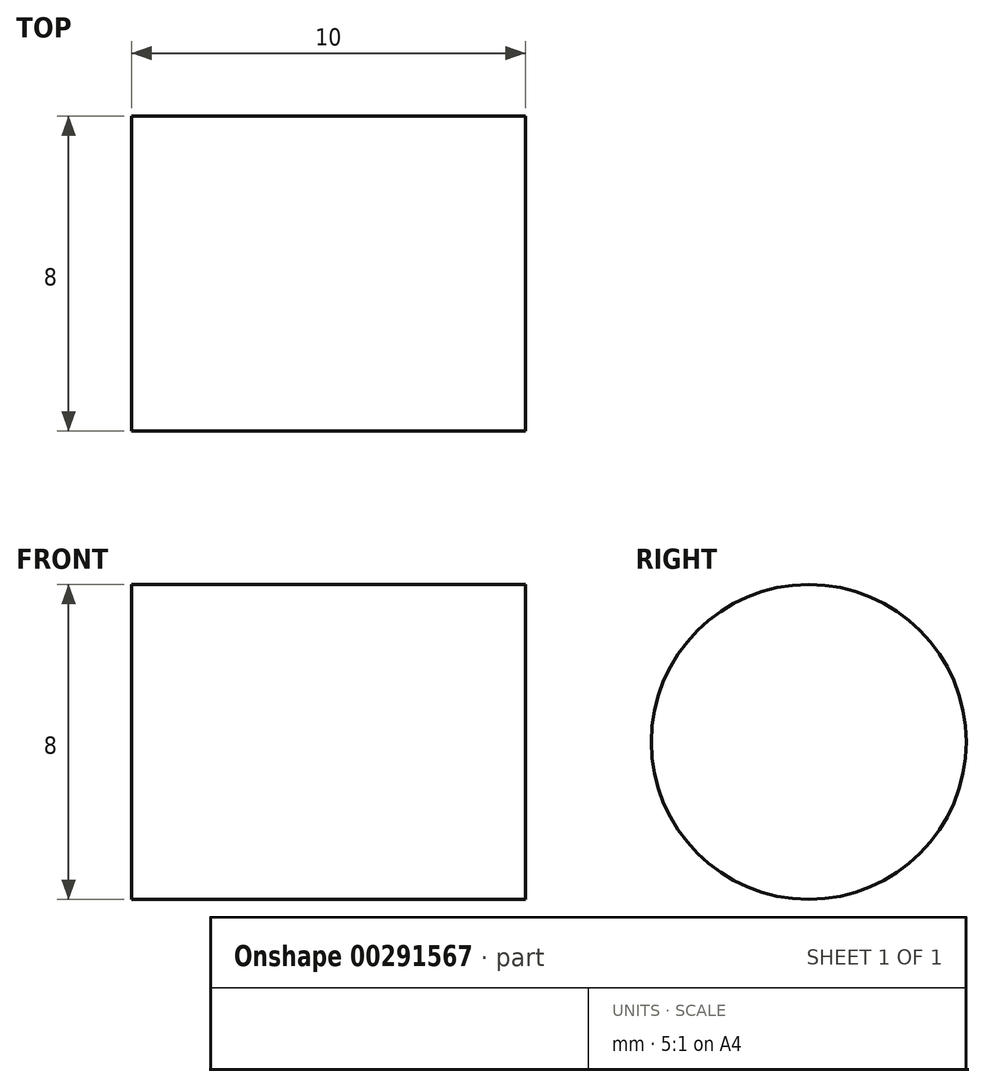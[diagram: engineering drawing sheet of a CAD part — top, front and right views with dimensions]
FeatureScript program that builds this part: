
annotation { "Feature Type Name" : "Feature", "Feature Type Description" : "" }
export const myFeature = defineFeature(function(context is Context, id is Id, definition is map)
    precondition{}
    {
        {
            var Q0;
            Q0=qCreatedBy(makeId("Right.planeOp"),FACE);
            var sketch = newSketch(context, id + "F0", { "sketchPlane" : qUnion([Q0])});
            skCircle(sketch, "E0", {"center": v(0, 0) * mm, "radius": 4 * mm});
            skSolve(sketch);
        }
        {
            var Q0;
            Q0 = qSketchRegion(id + "F0", true);
            extrude(context, id + "F1", {"entities" : qUnion([Q0]), "depth" : 10 * mm});
        }
    });
